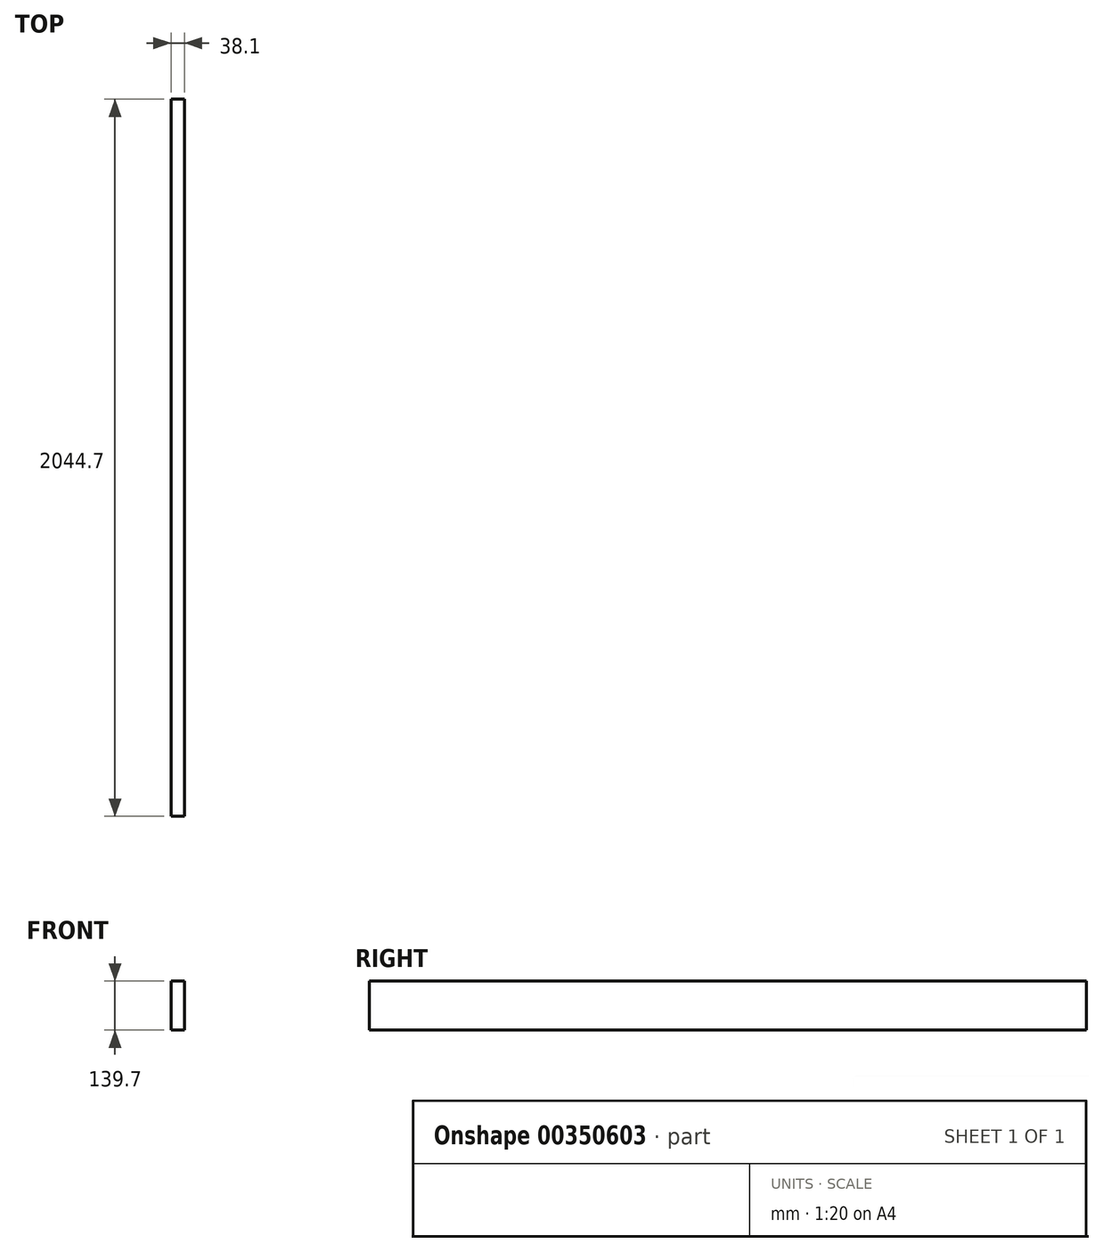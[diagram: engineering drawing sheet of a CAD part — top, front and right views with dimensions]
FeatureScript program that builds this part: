
annotation { "Feature Type Name" : "Feature", "Feature Type Description" : "" }
export const myFeature = defineFeature(function(context is Context, id is Id, definition is map)
    precondition{}
    {
        {
            var Q0;
            Q0=qCreatedBy(makeId("Top.planeOp"),FACE);
            var sketch = newSketch(context, id + "F0", { "sketchPlane" : qUnion([Q0])});
            skLineSegment(sketch, "E0.bottom", {"start": v(19.05, 1022.35) * mm, "end": v(-19.05, 1022.35) * mm});
            skLineSegment(sketch, "E0.top", {"start": v(19.05, -1022.35) * mm, "end": v(-19.05, -1022.35) * mm});
            skLineSegment(sketch, "E0.left", {"start": v(19.05, 1022.35) * mm, "end": v(19.05, -1022.35) * mm});
            skLineSegment(sketch, "E0.right", {"start": v(-19.05, 1022.35) * mm, "end": v(-19.05, -1022.35) * mm});
            skPoint(sketch, "E0.middle", {"position": v(0, 0) * mm});
            skSolve(sketch);
        }
        {
            var Q0;
            Q0=makeQuery(id+"F0.imprint","IMPRINT",FACE,{"disambiguationData":[TD([[makeQuery(id+"F0.imprint","IMPRINT",EDGE,{"derivedFrom":sQuery(id+"F0.wireOp",EDGE,"E0.bottom")}),1.0]])]});
            extrude(context, id + "F1", {"entities" : qUnion([Q0]), "depth" : 139.7 * mm});
        }
    });
